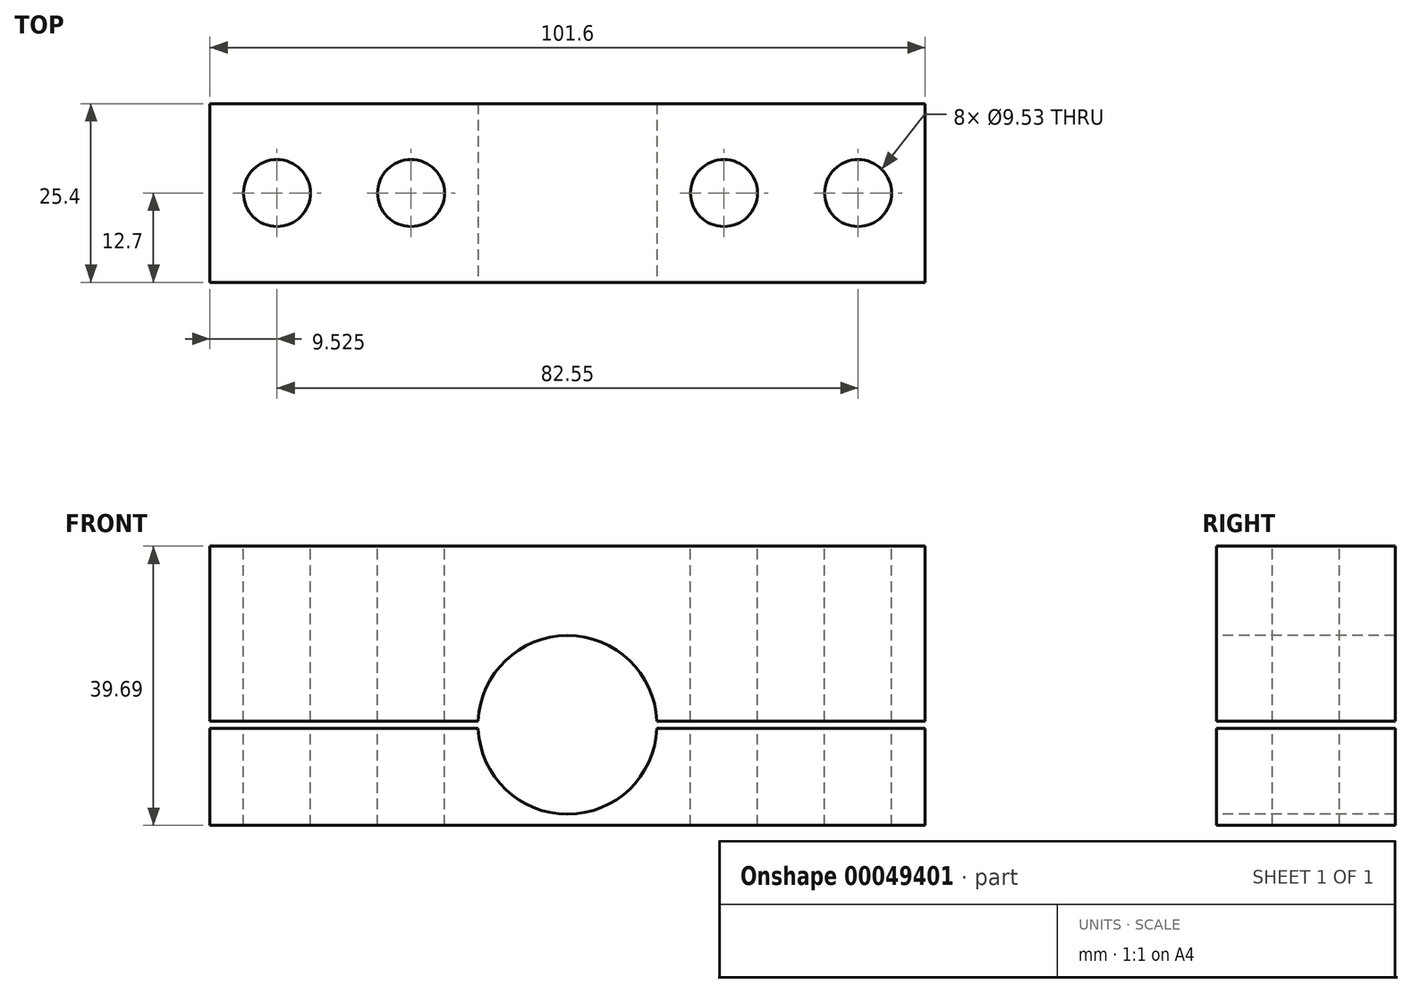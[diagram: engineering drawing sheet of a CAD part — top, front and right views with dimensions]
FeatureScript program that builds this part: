
annotation { "Feature Type Name" : "Feature", "Feature Type Description" : "" }
export const myFeature = defineFeature(function(context is Context, id is Id, definition is map)
    precondition{}
    {
        {
            var Q0;
            Q0=qCreatedBy(makeId("Front.planeOp"),FACE);
            var sketch = newSketch(context, id + "F0", { "sketchPlane" : qUnion([Q0])});
            skLineSegment(sketch, "E0.bottom", {"start": v(0, 0) * mm, "end": v(101.6, 0) * mm});
            skLineSegment(sketch, "E0.top", {"start": v(0, 49.21) * mm, "end": v(101.6, 49.21) * mm});
            skLineSegment(sketch, "E0.left", {"start": v(0, 0) * mm, "end": v(0, 49.21) * mm});
            skLineSegment(sketch, "E0.right", {"start": v(101.6, 0) * mm, "end": v(101.6, 49.21) * mm});
            skPoint(sketch, "E1.centerSnap0", {"position": v(50.8, 0) * mm});
            skSolve(sketch);
        }
        {
            var Q0;
            Q0 = qSketchRegion(id + "F0", true);
            extrude(context, id + "F1", {"entities" : qUnion([Q0]), "depth" : 25.4 * mm});
        }
        {
            var Q0;
            Q0=makeQuery(id+"F1.opExtrude","SWEPT_FACE",FACE,{"disambiguationData":[OSD([sQuery(id+"F0.wireOp",EDGE,"E0.top")])]});
            var sketch = newSketch(context, id + "F2", { "sketchPlane" : qUnion([Q0])});
            skCircle(sketch, "E2", {"center": v(9.53, -12.7) * mm, "radius": 4.76 * mm});
            skCircle(sketch, "E3", {"center": v(92.08, -12.7) * mm, "radius": 4.76 * mm});
            skCircle(sketch, "E4", {"center": v(28.58, -12.7) * mm, "radius": 4.76 * mm});
            skCircle(sketch, "E5", {"center": v(73.03, -12.7) * mm, "radius": 4.76 * mm});
            skSolve(sketch);
        }
        {
            var Q0;
            Q0 = qSketchRegion(id + "F2", true);
            extrude(context, id + "F3", {"entities" : qUnion([Q0]), "operationType" : NewBodyOperationType.REMOVE, "oppositeDirection" : true, "depth" : 50.17 * mm});
        }
        {
            var Q0;
            Q0=makeQuery(id+"F1.opExtrude","CAP_FACE",FACE,{"disambiguationData":[OSD([sQuery(id+"F0.wireOp",EDGE,"E0.bottom"),sQuery(id+"F0.wireOp",EDGE,"E0.top"),sQuery(id+"F0.wireOp",EDGE,"E0.left"),sQuery(id+"F0.wireOp",EDGE,"E0.right")])],"isStart":false});
            var sketch = newSketch(context, id + "F4", { "sketchPlane" : qUnion([Q0])});
            skCircle(sketch, "E6", {"center": v(50.8, 14.29) * mm, "radius": 12.7 * mm});
            skSolve(sketch);
        }
        {
            var Q0;
            Q0 = qSketchRegion(id + "F4", true);
            extrude(context, id + "F5", {"entities" : qUnion([Q0]), "operationType" : NewBodyOperationType.REMOVE, "endBound" : BoundingType.THROUGH_ALL, "oppositeDirection" : true, "depth" : 22.22 * mm});
        }
        {
            var Q0;
            Q0=makeQuery(id+"F1.opExtrude","CAP_FACE",FACE,{"disambiguationData":[OSD([sQuery(id+"F0.wireOp",EDGE,"E0.bottom"),sQuery(id+"F0.wireOp",EDGE,"E0.top"),sQuery(id+"F0.wireOp",EDGE,"E0.left"),sQuery(id+"F0.wireOp",EDGE,"E0.right")])],"isStart":true});
            var sketch = newSketch(context, id + "F6", { "sketchPlane" : qUnion([Q0])});
            skLineSegment(sketch, "E7", {"start": v(-50.8, 14.29) * mm, "end": v(-78.65, 14.29) * mm, "construction": true});
            skLineSegment(sketch, "E8.bottom", {"start": v(-101.6, 14.8) * mm, "end": v(0, 14.8) * mm});
            skLineSegment(sketch, "E8.top", {"start": v(-101.6, 13.78) * mm, "end": v(0, 13.78) * mm});
            skLineSegment(sketch, "E8.left", {"start": v(-101.6, 14.8) * mm, "end": v(-101.6, 13.78) * mm});
            skLineSegment(sketch, "E8.right", {"start": v(0, 14.8) * mm, "end": v(0, 13.78) * mm});
            skSolve(sketch);
        }
        {
            var Q0;
            Q0 = qSketchRegion(id + "F6", true);
            extrude(context, id + "F7", {"entities" : qUnion([Q0]), "operationType" : NewBodyOperationType.REMOVE, "endBound" : BoundingType.THROUGH_ALL, "oppositeDirection" : true, "depth" : 25.4 * mm});
        }
        {
            var Q0;
            {var subQ0=sQuery(id+"F0.wireOp",EDGE,"E0.right");var subQ1=sQuery(id+"F0.wireOp",EDGE,"E0.left");var subQ2=sQuery(id+"F0.wireOp",EDGE,"E0.top");Q0=makeQuery(id+"F7.boolean.opBoolean","SPLIT",FACE,{"disambiguationData":[TD([makeQuery(id+"F1.opExtrude","SWEPT_FACE",FACE,{"disambiguationData":[OSD([subQ2])]})])],"derivedFrom":makeQuery(id+"F1.opExtrude","CAP_FACE",FACE,{"disambiguationData":[OSD([sQuery(id+"F0.wireOp",EDGE,"E0.bottom"),subQ2,subQ1,subQ0])],"isStart":false})});}
            var sketch = newSketch(context, id + "F8", { "sketchPlane" : qUnion([Q0])});
            skLineSegment(sketch, "E9.bottom", {"start": v(-227.67, 155.26) * mm, "end": v(320.54, 155.26) * mm});
            skLineSegment(sketch, "E9.top", {"start": v(-227.67, 39.69) * mm, "end": v(320.54, 39.69) * mm});
            skLineSegment(sketch, "E9.left", {"start": v(-227.67, 155.26) * mm, "end": v(-227.67, 39.69) * mm});
            skLineSegment(sketch, "E9.right", {"start": v(320.54, 155.26) * mm, "end": v(320.54, 39.69) * mm});
            skSolve(sketch);
        }
        {
            var Q0;
            Q0 = qSketchRegion(id + "F8", true);
            extrude(context, id + "F9", {"entities" : qUnion([Q0]), "operationType" : NewBodyOperationType.REMOVE, "oppositeDirection" : true, "depth" : 25.4 * mm});
        }
    });
